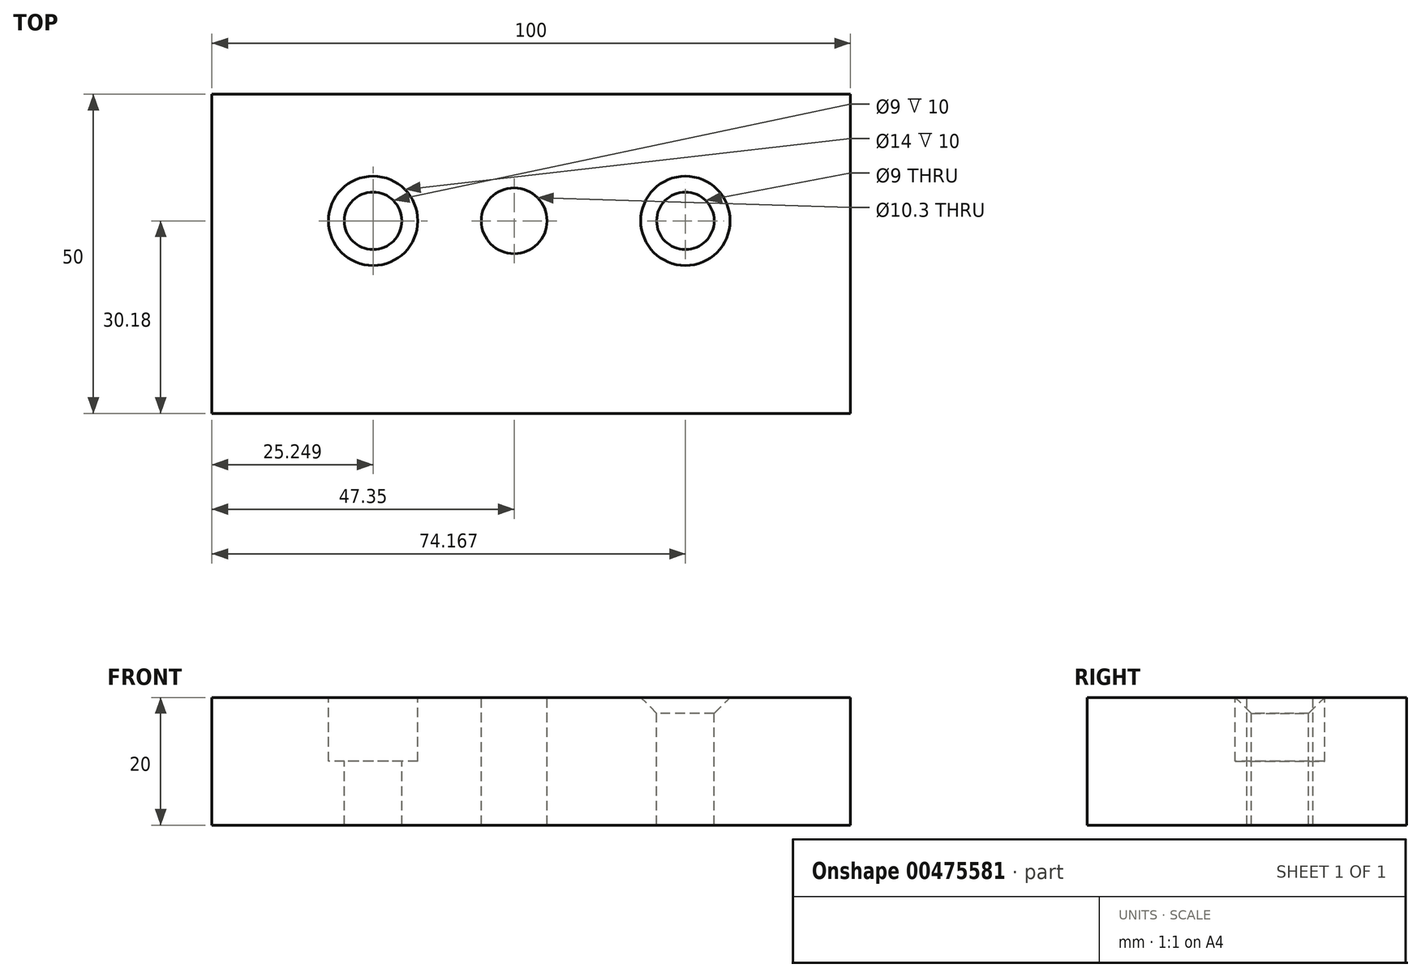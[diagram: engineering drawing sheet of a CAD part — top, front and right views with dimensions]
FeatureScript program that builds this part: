
annotation { "Feature Type Name" : "Feature", "Feature Type Description" : "" }
export const myFeature = defineFeature(function(context is Context, id is Id, definition is map)
    precondition{}
    {
        {
            var Q0;
            Q0=qCreatedBy(makeId("Top.planeOp"),FACE);
            var sketch = newSketch(context, id + "F0", { "sketchPlane" : qUnion([Q0])});
            skLineSegment(sketch, "E0.bottom", {"start": v(-30.6, 19.82) * mm, "end": v(69.4, 19.82) * mm});
            skLineSegment(sketch, "E0.top", {"start": v(-30.6, -30.18) * mm, "end": v(69.4, -30.18) * mm});
            skLineSegment(sketch, "E0.left", {"start": v(-30.6, 19.82) * mm, "end": v(-30.6, -30.18) * mm});
            skLineSegment(sketch, "E0.right", {"start": v(69.4, 19.82) * mm, "end": v(69.4, -30.18) * mm});
            skSolve(sketch);
        }
        {
            var Q0;
            Q0=makeQuery(id+"F0.imprint","IMPRINT",FACE,{"disambiguationData":[TD([[makeQuery(id+"F0.imprint","IMPRINT",EDGE,{"derivedFrom":sQuery(id+"F0.wireOp",EDGE,"E0.bottom")}),-1.0]])]});
            extrude(context, id + "F1", {"entities" : qUnion([Q0]), "depth" : 20 * mm});
        }
        {
            var Q0;
            Q0=makeQuery(id+"F1.opExtrude","CAP_FACE",FACE,{"disambiguationData":[OSD([sQuery(id+"F0.wireOp",EDGE,"E0.bottom"),sQuery(id+"F0.wireOp",EDGE,"E0.top"),sQuery(id+"F0.wireOp",EDGE,"E0.left"),sQuery(id+"F0.wireOp",EDGE,"E0.right")])],"isStart":false});
            var sketch = newSketch(context, id + "F2", { "sketchPlane" : qUnion([Q0])});
            skPoint(sketch, "E1", {"position": v(-5.36, 0) * mm});
            skPoint(sketch, "E2", {"position": v(43.56, 0) * mm});
            skPoint(sketch, "E3", {"position": v(16.74, 0) * mm});
            skSolve(sketch);
        }
        {
            var Q0;
            Q0=sQuery(id+"F2.wireOp",VERTEX,"E1");
            var Q1;
            Q1=makeQuery(id+"F1.opExtrude","SWEPT_BODY",BODY,{"disambiguationData":[OSD([sQuery(id+"F0.wireOp",EDGE,"E0.bottom"),sQuery(id+"F0.wireOp",EDGE,"E0.top"),sQuery(id+"F0.wireOp",EDGE,"E0.left"),sQuery(id+"F0.wireOp",EDGE,"E0.right")])]});
            hole(context, id + "F3", {"style" : HoleStyle.C_BORE, "endStyle" : HoleEndStyle.BLIND, "holeDiameter" : 9 * mm, "cBoreDiameter" : 14 * mm, "cBoreDepth" : 10 * mm, "holeDepth" : 30 * mm, "isTappedThrough" : true, "tappedDepth" : 12 * mm, "tapClearance" : 3, "locations" : qUnion([Q0]), "scope" : qUnion([Q1])});
        }
        {
            var Q0;
            Q0=sQuery(id+"F2.wireOp",VERTEX,"E2");
            var Q1;
            Q1=makeQuery(id+"F1.opExtrude","SWEPT_BODY",BODY,{"disambiguationData":[OSD([sQuery(id+"F0.wireOp",EDGE,"E0.bottom"),sQuery(id+"F0.wireOp",EDGE,"E0.top"),sQuery(id+"F0.wireOp",EDGE,"E0.left"),sQuery(id+"F0.wireOp",EDGE,"E0.right")])]});
            hole(context, id + "F4", {"style" : HoleStyle.C_SINK, "endStyle" : HoleEndStyle.THROUGH, "holeDiameter" : 9 * mm, "cSinkDiameter" : 14 * mm, "cSinkAngle" : 90 * degree, "isTappedThrough" : true, "tappedDepth" : 12 * mm, "tapClearance" : 3, "locations" : qUnion([Q0]), "scope" : qUnion([Q1])});
        }
        {
            var Q0;
            Q0=sQuery(id+"F2.wireOp",VERTEX,"E3");
            var Q1;
            Q1=makeQuery(id+"F1.opExtrude","SWEPT_BODY",BODY,{"disambiguationData":[OSD([sQuery(id+"F0.wireOp",EDGE,"E0.bottom"),sQuery(id+"F0.wireOp",EDGE,"E0.top"),sQuery(id+"F0.wireOp",EDGE,"E0.left"),sQuery(id+"F0.wireOp",EDGE,"E0.right")])]});
            hole(context, id + "F5", {"style" : HoleStyle.SIMPLE, "endStyle" : HoleEndStyle.THROUGH, "standardTappedOrClearance" : lookupTablePath({ "standard" : "ISO", "engagement" : "75%", "pitch" : "1.75 mm", "size" : "M12", "type" : "Tapped" }), "standardBlindInLast" : lookupTablePath({ "standard" : "ISO", "engagement" : "75%", "pitch" : "1.75 mm", "size" : "M12", "type" : "Tapped" }), "holeDiameter" : 10.3 * mm, "showTappedDepth" : true, "isTappedThrough" : true, "tappedDepth" : 12 * mm, "tapClearance" : 3, "locations" : qUnion([Q0]), "scope" : qUnion([Q1]), "majorDiameter" : 12 * mm});
        }
    });
